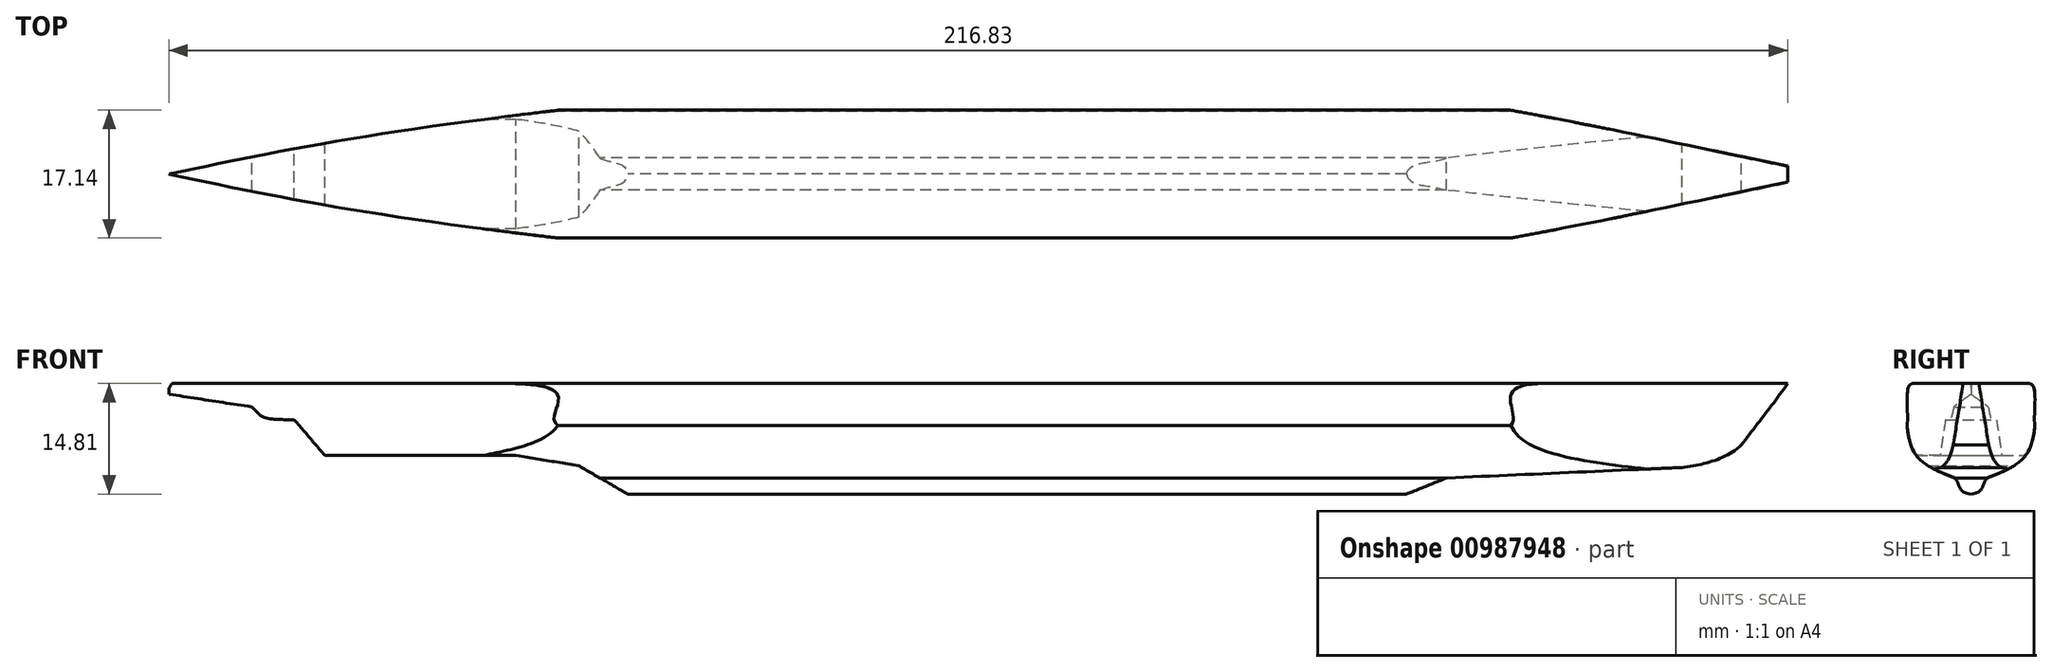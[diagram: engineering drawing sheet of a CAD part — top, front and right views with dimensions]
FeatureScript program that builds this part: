
annotation { "Feature Type Name" : "Feature", "Feature Type Description" : "" }
export const myFeature = defineFeature(function(context is Context, id is Id, definition is map)
    precondition{}
    {
        {
            var Q0;
            Q0=qCreatedBy(makeId("Front.planeOp"),FACE);
            var sketch = newSketch(context, id + "F0", { "sketchPlane" : qUnion([Q0])});
            skLineSegment(sketch, "E0", {"start": v(80.83, -11.25) * mm, "end": v(49.3, -12.66) * mm});
            skLineSegment(sketch, "E1", {"start": v(49.3, -12.66) * mm, "end": v(43.88, -14.84) * mm});
            skLineSegment(sketch, "E2", {"start": v(43.88, -14.84) * mm, "end": v(-60.33, -14.84) * mm});
            skLineSegment(sketch, "E3", {"start": v(-60.33, -14.84) * mm, "end": v(-66.93, -11.03) * mm});
            skLineSegment(sketch, "E4", {"start": v(-66.93, -11.03) * mm, "end": v(-75.33, -9.62) * mm});
            skLineSegment(sketch, "E5", {"start": v(-75.33, -9.62) * mm, "end": v(-100.97, -9.62) * mm});
            skLineSegment(sketch, "E6", {"start": v(-100.97, -9.62) * mm, "end": v(-105.05, -4.84) * mm});
            skLineSegment(sketch, "E7", {"start": v(-110.75, -3.13) * mm, "end": v(-121.84, -1.43) * mm});
            skLineSegment(sketch, "E8", {"start": v(-120.28, 1.85) * mm, "end": v(-108.03, 2.33) * mm});
            skLineSegment(sketch, "E9", {"start": v(-108.03, 2.33) * mm, "end": v(-107.8, 2.57) * mm});
            skLineSegment(sketch, "E10", {"start": v(-107.8, 2.57) * mm, "end": v(-40.45, 2.57) * mm});
            skLineSegment(sketch, "E11", {"start": v(-40.45, 2.57) * mm, "end": v(35.03, 1.85) * mm});
            skLineSegment(sketch, "E12", {"start": v(35.03, 1.85) * mm, "end": v(94.1, 3.92) * mm});
            skFitSpline(sketch, "E13", {"points": [v(96.2, 1.85) * mm, v(94.1, 3.92) * mm], "startDerivative": vector(1.21, 4.6) * mm, "endDerivative": vector(-4.59, -0.89) * mm});
            skFitSpline(sketch, "E14", {"points": [v(88.8, -8.26) * mm, v(80.83, -11.25) * mm], "startDerivative": vector(-6.46, -5.74) * mm, "endDerivative": vector(-8.64, -0.97) * mm});
            skFitSpline(sketch, "E15", {"points": [v(96.2, 1.85) * mm, v(88.8, -8.26) * mm], "startDerivative": vector(-7.05, -11.27) * mm, "endDerivative": vector(-7.4, -10.1) * mm});
            skFitSpline(sketch, "E16", {"points": [v(-105.05, -4.84) * mm, v(-110.75, -3.13) * mm], "startDerivative": vector(-12.9, 0) * mm, "endDerivative": vector(-4.41, 4.59) * mm});
            skLineSegment(sketch, "E17", {"start": v(-121.84, -1.43) * mm, "end": v(-121.84, -0.64) * mm});
            skLineSegment(sketch, "E18", {"start": v(-121.84, -0.64) * mm, "end": v(-120.28, 1.85) * mm});
            skSolve(sketch);
        }
        {
            var Q0;
            Q0=qCreatedBy(makeId("Top.planeOp"),FACE);
            var sketch = newSketch(context, id + "F1", { "sketchPlane" : qUnion([Q0])});
            skLineSegment(sketch, "E19", {"start": v(-121.84, 0) * mm, "end": v(100.18, 0) * mm, "construction": true});
            skLineSegment(sketch, "E20", {"start": v(46.25, 10.53) * mm, "end": v(46.25, 0) * mm, "construction": true});
            skLineSegment(sketch, "E21", {"start": v(-3.4, 0) * mm, "end": v(-3.4, 13.58) * mm, "construction": true});
            skLineSegment(sketch, "E22", {"start": v(-26.42, 0) * mm, "end": v(-26.42, 12.51) * mm, "construction": true});
            skLineSegment(sketch, "E23", {"start": v(-54.31, 0) * mm, "end": v(-54.31, 10.21) * mm, "construction": true});
            skLineSegment(sketch, "E24", {"start": v(-86.88, 0) * mm, "end": v(-86.88, 6.36) * mm, "construction": true});
            skFitSpline(sketch, "E25", {"points": [v(-121.84, 0) * mm, v(-86.88, 6.36) * mm, v(-3.4, 13.58) * mm, v(46.25, 10.53) * mm, v(100.18, 0) * mm], "startDerivative": vector(143.56, 30.8) * mm, "endDerivative": vector(245.9, -50.8) * mm});
            skFitSpline(sketch, "E26.MirrorCS", {"points": [v(-121.84, 0) * mm, v(-86.88, -6.36) * mm, v(-3.4, -13.58) * mm, v(46.25, -10.53) * mm, v(100.18, 0) * mm], "startDerivative": vector(143.56, -30.8) * mm, "endDerivative": vector(245.9, 50.8) * mm});
            skSolve(sketch);
        }
        {
            var Q0;
            Q0=makeQuery(id+"F0.imprint","IMPRINT",FACE,{"disambiguationData":[TD([[makeQuery(id+"F0.imprint","IMPRINT",EDGE,{"derivedFrom":sQuery(id+"F0.wireOp",EDGE,"E0")}),-1.0]])]});
            extrude(context, id + "F2", {"entities" : qUnion([Q0]), "depth" : 25.4 * mm, "offsetDistance" : 25.4 * mm, "hasSecondDirection" : true, "secondDirectionOppositeDirection" : true, "secondDirectionDepth" : 25.4 * mm});
        }
        {
            var Q0;
            Q0=makeQuery(id+"F1.imprint","IMPRINT",FACE,{"disambiguationData":[TD([[makeQuery(id+"F1.imprint","IMPRINT",EDGE,{"derivedFrom":sQuery(id+"F1.wireOp",EDGE,"E25")}),-1.0]])]});
            extrude(context, id + "F3", {"entities" : qUnion([Q0]), "operationType" : NewBodyOperationType.INTERSECT, "depth" : 25.4 * mm, "offsetDistance" : 25.4 * mm, "hasSecondDirection" : true, "secondDirectionOppositeDirection" : true, "secondDirectionDepth" : 25.4 * mm});
        }
        {
            var Q0;
            Q0=qCreatedBy(makeId("Right.planeOp"),FACE);
            var sketch = newSketch(context, id + "F4", { "sketchPlane" : qUnion([Q0])});
            skLineSegment(sketch, "E27", {"start": v(0, -14.9) * mm, "end": v(0, 3.73) * mm, "construction": true});
            skLineSegment(sketch, "E28.bottom", {"start": v(0, -14.81) * mm, "end": v(-2.16, -14.81) * mm, "construction": true});
            skLineSegment(sketch, "E28.top", {"start": v(0, -12.66) * mm, "end": v(-2.16, -12.66) * mm});
            skLineSegment(sketch, "E28.left", {"start": v(0, -14.81) * mm, "end": v(0, -12.66) * mm});
            skLineSegment(sketch, "E28.right", {"start": v(-2.16, -14.81) * mm, "end": v(-2.16, -12.66) * mm, "construction": true});
            skFitSpline(sketch, "E29", {"points": [v(-2.16, -12.66) * mm, v(0, -14.81) * mm], "startDerivative": vector(2.16, -2.15) * mm, "endDerivative": vector(5.44, -0.28) * mm});
            skLineSegment(sketch, "E30.bottom", {"start": v(0, -12.66) * mm, "end": v(-8.56, -12.66) * mm, "construction": true});
            skLineSegment(sketch, "E30.top", {"start": v(0, -5.65) * mm, "end": v(-8.56, -5.65) * mm});
            skLineSegment(sketch, "E30.left", {"start": v(0, -12.66) * mm, "end": v(0, -5.65) * mm});
            skLineSegment(sketch, "E30.right", {"start": v(-8.56, -12.66) * mm, "end": v(-8.56, -5.65) * mm, "construction": true});
            skFitSpline(sketch, "E31", {"points": [v(-2.16, -12.66) * mm, v(-8.56, -5.65) * mm], "startDerivative": vector(-10.84, 4.43) * mm, "endDerivative": vector(-1.04, 14.57) * mm});
            skLineSegment(sketch, "E32.bottom", {"start": v(0, 0) * mm, "end": v(-8.58, 0) * mm});
            skLineSegment(sketch, "E32.top", {"start": v(0, 1.78) * mm, "end": v(-8.58, 1.78) * mm, "construction": true});
            skLineSegment(sketch, "E32.left", {"start": v(0, 0) * mm, "end": v(0, 1.78) * mm, "construction": true});
            skLineSegment(sketch, "E32.right", {"start": v(-8.58, 0) * mm, "end": v(-8.58, 1.78) * mm, "construction": true});
            skFitSpline(sketch, "E33", {"points": [v(-8.56, -5.65) * mm, v(-7.75, 0) * mm], "startDerivative": vector(0.8, 5.65) * mm, "endDerivative": vector(4.13, 0) * mm});
            skLineSegment(sketch, "E34", {"start": v(-7.75, 0) * mm, "end": v(0, 0) * mm});
            skFitSpline(sketch, "E35.MirrorCS", {"points": [v(2.16, -12.66) * mm, v(8.56, -5.65) * mm], "startDerivative": vector(10.84, 4.43) * mm, "endDerivative": vector(1.04, 14.57) * mm});
            skFitSpline(sketch, "E36.MirrorCS", {"points": [v(2.16, -12.66) * mm, v(0, -14.81) * mm], "startDerivative": vector(-2.16, -2.15) * mm, "endDerivative": vector(-5.44, -0.28) * mm});
            skFitSpline(sketch, "E37.MirrorCS", {"points": [v(8.56, -5.65) * mm, v(7.75, 0) * mm], "startDerivative": vector(-0.8, 5.65) * mm, "endDerivative": vector(-4.13, 0) * mm});
            skLineSegment(sketch, "E38.MirrorCS", {"start": v(0, 0) * mm, "end": v(8.58, 0) * mm});
            skLineSegment(sketch, "E39.MirrorCS", {"start": v(0, 0) * mm, "end": v(8.58, 0) * mm, "construction": true});
            skSolve(sketch);
        }
        {
            var Q0;
            Q0 = qSketchRegion(id + "F4", true);
            extrude(context, id + "F5", {"entities" : qUnion([Q0]), "operationType" : NewBodyOperationType.INTERSECT, "depth" : 127 * mm, "offsetDistance" : 25.4 * mm, "hasSecondDirection" : true, "secondDirectionOppositeDirection" : true, "secondDirectionDepth" : 127 * mm});
        }
    });
